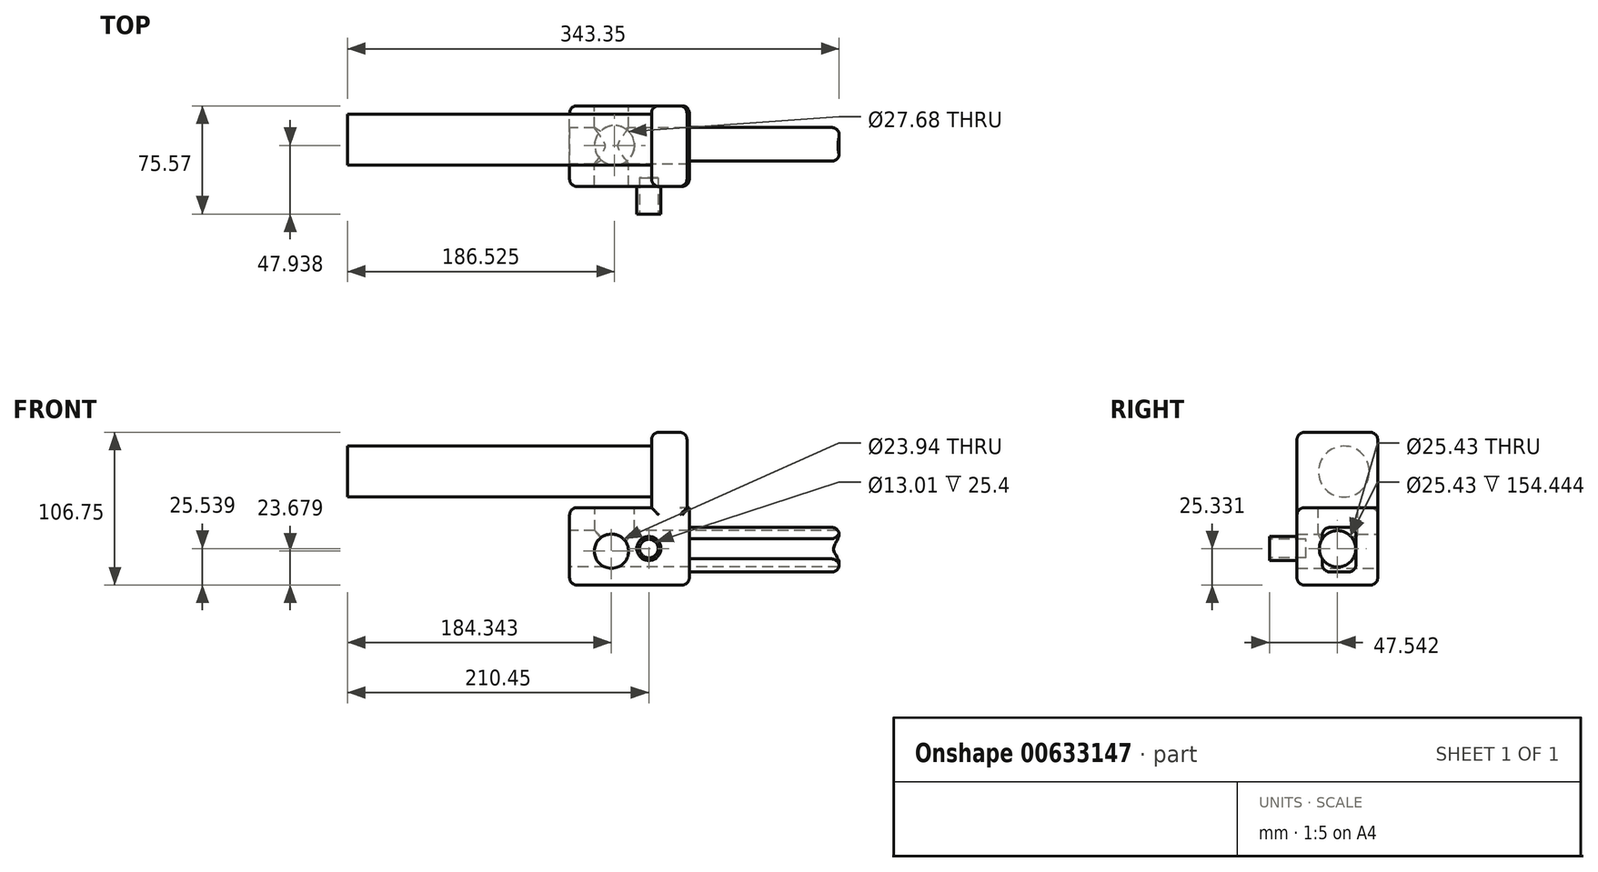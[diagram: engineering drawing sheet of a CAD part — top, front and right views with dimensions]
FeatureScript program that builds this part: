
annotation { "Feature Type Name" : "Feature", "Feature Type Description" : "" }
export const myFeature = defineFeature(function(context is Context, id is Id, definition is map)
    precondition{}
    {
        {
            var Q0;
            Q0=qCreatedBy(makeId("Front.planeOp"),FACE);
            var sketch = newSketch(context, id + "F0", { "sketchPlane" : qUnion([Q0])});
            skLineSegment(sketch, "E0.bottom", {"start": v(-35.66, -9.17) * mm, "end": v(47.91, -9.17) * mm});
            skLineSegment(sketch, "E0.top", {"start": v(-35.66, 44.89) * mm, "end": v(47.91, 44.89) * mm});
            skLineSegment(sketch, "E0.left", {"start": v(-35.66, -9.17) * mm, "end": v(-35.66, 44.89) * mm});
            skLineSegment(sketch, "E0.right", {"start": v(47.91, -9.17) * mm, "end": v(47.91, 44.89) * mm});
            skLineSegment(sketch, "E1.bottom", {"start": v(21.55, 44.89) * mm, "end": v(46.28, 44.89) * mm});
            skLineSegment(sketch, "E1.top", {"start": v(21.55, 97.58) * mm, "end": v(46.28, 97.58) * mm});
            skLineSegment(sketch, "E1.left", {"start": v(21.55, 44.89) * mm, "end": v(21.55, 97.58) * mm});
            skLineSegment(sketch, "E1.right", {"start": v(46.28, 44.89) * mm, "end": v(46.28, 97.58) * mm});
            skSolve(sketch);
        }
        {
            var Q0;
            Q0 = qSketchRegion(id + "F0", true);
            extrude(context, id + "F1", {"entities" : qUnion([Q0]), "depth" : 56.33 * mm, "offsetDistance" : 25.4 * mm});
        }
        {
            var Q0;
            Q0=makeQuery(id+"F1.opExtrude","CAP_EDGE",EDGE,{"disambiguationData":[OSD([sQuery(id+"F0.wireOp",EDGE,"E1.left")])],"isStart":false});
            var Q1;
            Q1=makeQuery(id+"F1.opExtrude","CAP_EDGE",EDGE,{"disambiguationData":[OSD([sQuery(id+"F0.wireOp",EDGE,"E1.right")])],"isStart":false});
            var Q2;
            Q2=makeQuery(id+"F1.opExtrude","CAP_EDGE",EDGE,{"disambiguationData":[OSD([sQuery(id+"F0.wireOp",EDGE,"E1.right")])],"isStart":true});
            var Q3;
            Q3=makeQuery(id+"F1.opExtrude","CAP_EDGE",EDGE,{"disambiguationData":[OSD([sQuery(id+"F0.wireOp",EDGE,"E1.left")])],"isStart":true});
            var Q4;
            Q4=makeQuery(id+"F1.opExtrude","CAP_EDGE",EDGE,{"disambiguationData":[OSD([sQuery(id+"F0.wireOp",EDGE,"E0.bottom")])],"isStart":false});
            var Q5;
            Q5=makeQuery(id+"F1.opExtrude","CAP_FACE",FACE,{"disambiguationData":[OSD([sQuery(id+"F0.wireOp",EDGE,"E0.bottom"),sQuery(id+"F0.wireOp",EDGE,"E0.top"),sQuery(id+"F0.wireOp",EDGE,"E0.left"),sQuery(id+"F0.wireOp",EDGE,"E0.right"),sQuery(id+"F0.wireOp",EDGE,"E1.top"),sQuery(id+"F0.wireOp",EDGE,"E1.left"),sQuery(id+"F0.wireOp",EDGE,"E1.right")])],"isStart":false});
            var Q6;
            Q6=makeQuery(id+"F1.opExtrude","CAP_EDGE",EDGE,{"disambiguationData":[OSD([sQuery(id+"F0.wireOp",EDGE,"E0.left")])],"isStart":true});
            var Q7;
            Q7=makeQuery(id+"F1.opExtrude","SWEPT_EDGE",EDGE,{"disambiguationData":[OSD([sQuery(id+"F0.wireOp",EDGE,"E1.top"),sQuery(id+"F0.wireOp",EDGE,"E1.left")])]});
            var Q8;
            Q8=makeQuery(id+"F1.opExtrude","SWEPT_EDGE",EDGE,{"disambiguationData":[OSD([sQuery(id+"F0.wireOp",EDGE,"E1.top"),sQuery(id+"F0.wireOp",EDGE,"E1.right")])]});
            fillet(context, id + "F2", {"entities" : qUnion([Q0, Q1, Q2, Q3, Q4, Q5, Q6, Q7, Q8]), "radius" : 5.08 * mm, "tangentPropagation" : true, "allowEdgeOverflow" : false});
        }
        {
            var Q0;
            Q0=makeQuery(id+"F1.opExtrude","CAP_EDGE",EDGE,{"disambiguationData":[OSD([sQuery(id+"F0.wireOp",EDGE,"E0.bottom")])],"isStart":true});
            var Q1;
            Q1=makeQuery(id+"F1.opExtrude","SWEPT_EDGE",EDGE,{"disambiguationData":[OSD([sQuery(id+"F0.wireOp",EDGE,"E0.bottom"),sQuery(id+"F0.wireOp",EDGE,"E0.right")])]});
            var Q2;
            Q2=makeQuery(id+"F1.opExtrude","SWEPT_EDGE",EDGE,{"disambiguationData":[OSD([sQuery(id+"F0.wireOp",EDGE,"E0.bottom"),sQuery(id+"F0.wireOp",EDGE,"E0.left")])]});
            fillet(context, id + "F3", {"entities" : qUnion([Q0, Q1, Q2]), "radius" : 5.08 * mm, "tangentPropagation" : true, "allowEdgeOverflow" : false});
        }
        {
            var Q0;
            Q0=makeQuery(id+"F1.opExtrude","CAP_FACE",FACE,{"disambiguationData":[OSD([sQuery(id+"F0.wireOp",EDGE,"E0.bottom"),sQuery(id+"F0.wireOp",EDGE,"E0.top"),sQuery(id+"F0.wireOp",EDGE,"E0.left"),sQuery(id+"F0.wireOp",EDGE,"E0.right"),sQuery(id+"F0.wireOp",EDGE,"E1.top"),sQuery(id+"F0.wireOp",EDGE,"E1.left"),sQuery(id+"F0.wireOp",EDGE,"E1.right")])],"isStart":true});
            var sketch = newSketch(context, id + "F4", { "sketchPlane" : qUnion([Q0])});
            skCircle(sketch, "E2", {"center": v(-20.36, 19.85) * mm, "radius": 0.17 * mm});
            skCircle(sketch, "E3", {"center": v(-19.66, 16.37) * mm, "radius": 8.38 * mm});
            skSolve(sketch);
        }
        {
            var Q0;
            Q0=makeQuery(id+"F4.imprint","IMPRINT",FACE,{"disambiguationData":[TD([[makeQuery(id+"F4.imprint","IMPRINT",EDGE,{"derivedFrom":sQuery(id+"F4.wireOp",EDGE,"E2")}),-1.0]])]});
            extrude(context, id + "F5", {"entities" : qUnion([Q0]), "operationType" : NewBodyOperationType.ADD, "oppositeDirection" : true, "depth" : 75.57 * mm, "offsetDistance" : 25.4 * mm});
        }
        {
            var Q0;
            Q0=makeQuery(id+"F5.opExtrude","CAP_FACE",FACE,{"disambiguationData":[OSD([sQuery(id+"F4.wireOp",EDGE,"E2"),sQuery(id+"F4.wireOp",EDGE,"E3")])],"isStart":false});
            var sketch = newSketch(context, id + "F6", { "sketchPlane" : qUnion([Q0])});
            skCircle(sketch, "E4", {"center": v(19.66, 16.37) * mm, "radius": 6.5 * mm});
            skSolve(sketch);
        }
        {
            var Q0;
            Q0 = qSketchRegion(id + "F6", true);
            extrude(context, id + "F7", {"entities" : qUnion([Q0]), "operationType" : NewBodyOperationType.REMOVE, "oppositeDirection" : true, "depth" : 25.4 * mm, "offsetDistance" : 25.4 * mm});
        }
        {
            var Q0;
            Q0=makeQuery(id+"F1.opExtrude","CAP_EDGE",EDGE,{"disambiguationData":[OSD([sQuery(id+"F0.wireOp",EDGE,"E1.top")])],"isStart":true});
            fillet(context, id + "F8", {"entities" : qUnion([Q0]), "radius" : 5.08 * mm, "tangentPropagation" : true, "allowEdgeOverflow" : false});
        }
        {
            var Q0;
            Q0=makeQuery(id+"F1.opExtrude","CAP_EDGE",EDGE,{"disambiguationData":[OSD([sQuery(id+"F0.wireOp",EDGE,"E0.right")])],"isStart":true});
            fillet(context, id + "F9", {"entities" : qUnion([Q0]), "radius" : 5.08 * mm, "tangentPropagation" : true, "allowEdgeOverflow" : false});
        }
        {
            var Q0;
            {var subQ0=sQuery(id+"F0.wireOp",EDGE,"E0.top");Q0=makeQuery(id+"F1.opExtrude","CAP_EDGE",EDGE,{"disambiguationData":[OSD([subQ0]),TDD([makeQuery(id+"F0.imprint","IMPRINT",EDGE,{"disambiguationData":[TD([[makeQuery(id+"F0.imprint","INTERSECT",VERTEX,{"derivedFrom":[subQ0,sQuery(id+"F0.wireOp",EDGE,"E0.left")]}),-1.0]])],"derivedFrom":subQ0})])],"isStart":true});}
            fillet(context, id + "F10", {"entities" : qUnion([Q0]), "radius" : 5.08 * mm, "tangentPropagation" : true, "allowEdgeOverflow" : false});
        }
        {
            var Q0;
            Q0=makeQuery(id+"F1.opExtrude","SWEPT_FACE",FACE,{"disambiguationData":[OSD([sQuery(id+"F0.wireOp",EDGE,"E0.right")])]});
            var sketch = newSketch(context, id + "F11", { "sketchPlane" : qUnion([Q0])});
            skSolve(sketch);
        }
        {
            var Q0;
            {var subQ0=sQuery(id+"F0.wireOp",EDGE,"E0.right");var subQ1=makeQuery(id+"F1.opExtrude","SWEPT_FACE",FACE,{"disambiguationData":[OSD([subQ0])]});Q0=makeQuery(id+"F11.imprint","IMPRINT",FACE,{"disambiguationData":[TD([[makeQuery(id+"F11.imprint","IMPRINT",EDGE,{"derivedFrom":makeQuery(id+"F2.opFillet","BLEND_EDGE",EDGE,{"blendedFrom":[makeQuery(id+"F1.opExtrude","CAP_EDGE",EDGE,{"disambiguationData":[OSD([subQ0])],"isStart":false}),subQ1],"blendedInto":[subQ1]})}),1.0]])]});}
            var sketch = newSketch(context, id + "F12", { "sketchPlane" : qUnion([Q0])});
            skLineSegment(sketch, "E5.bottom", {"start": v(-38.61, 31.08) * mm, "end": v(-15.2, 31.08) * mm});
            skLineSegment(sketch, "E5.top", {"start": v(-38.61, 0) * mm, "end": v(-15.2, 0) * mm});
            skLineSegment(sketch, "E5.left", {"start": v(-38.61, 31.08) * mm, "end": v(-38.61, 0) * mm});
            skLineSegment(sketch, "E5.right", {"start": v(-15.2, 31.08) * mm, "end": v(-15.2, 0) * mm});
            skSolve(sketch);
        }
        {
            var Q0;
            Q0 = qSketchRegion(id + "F12", true);
            extrude(context, id + "F13", {"entities" : qUnion([Q0]), "operationType" : NewBodyOperationType.ADD, "depth" : 104.65 * mm, "offsetDistance" : 25.4 * mm});
        }
        {
            var Q0;
            Q0=makeQuery(id+"F13.opExtrude","CAP_EDGE",EDGE,{"disambiguationData":[OSD([sQuery(id+"F12.wireOp",EDGE,"E5.left")])],"isStart":false});
            var Q1;
            Q1=makeQuery(id+"F13.opExtrude","CAP_EDGE",EDGE,{"disambiguationData":[OSD([sQuery(id+"F12.wireOp",EDGE,"E5.bottom")])],"isStart":false});
            var Q2;
            Q2=makeQuery(id+"F13.opExtrude","CAP_EDGE",EDGE,{"disambiguationData":[OSD([sQuery(id+"F12.wireOp",EDGE,"E5.right")])],"isStart":false});
            var Q3;
            Q3=makeQuery(id+"F13.opExtrude","CAP_EDGE",EDGE,{"disambiguationData":[OSD([sQuery(id+"F12.wireOp",EDGE,"E5.top")])],"isStart":false});
            var Q4;
            Q4=makeQuery(id+"F13.opExtrude","SWEPT_EDGE",EDGE,{"disambiguationData":[OSD([sQuery(id+"F12.wireOp",EDGE,"E5.bottom"),sQuery(id+"F12.wireOp",EDGE,"E5.left")])]});
            var Q5;
            Q5=makeQuery(id+"F13.opExtrude","SWEPT_EDGE",EDGE,{"disambiguationData":[OSD([sQuery(id+"F12.wireOp",EDGE,"E5.bottom"),sQuery(id+"F12.wireOp",EDGE,"E5.right")])]});
            var Q6;
            Q6=makeQuery(id+"F13.opExtrude","SWEPT_EDGE",EDGE,{"disambiguationData":[OSD([sQuery(id+"F12.wireOp",EDGE,"E5.top"),sQuery(id+"F12.wireOp",EDGE,"E5.left")])]});
            var Q7;
            Q7=makeQuery(id+"F13.opExtrude","SWEPT_EDGE",EDGE,{"disambiguationData":[OSD([sQuery(id+"F12.wireOp",EDGE,"E5.top"),sQuery(id+"F12.wireOp",EDGE,"E5.right")])]});
            fillet(context, id + "F14", {"entities" : qUnion([Q0, Q1, Q2, Q3, Q4, Q5, Q6, Q7]), "radius" : 5.08 * mm, "tangentPropagation" : true, "allowEdgeOverflow" : false});
        }
        {
            var Q0;
            Q0=makeQuery(id+"F1.opExtrude","CAP_FACE",FACE,{"disambiguationData":[OSD([sQuery(id+"F0.wireOp",EDGE,"E0.bottom"),sQuery(id+"F0.wireOp",EDGE,"E0.top"),sQuery(id+"F0.wireOp",EDGE,"E0.left"),sQuery(id+"F0.wireOp",EDGE,"E0.right"),sQuery(id+"F0.wireOp",EDGE,"E1.top"),sQuery(id+"F0.wireOp",EDGE,"E1.left"),sQuery(id+"F0.wireOp",EDGE,"E1.right")])],"isStart":true});
            var sketch = newSketch(context, id + "F15", { "sketchPlane" : qUnion([Q0])});
            skCircle(sketch, "E6", {"center": v(6.45, 14.5) * mm, "radius": 11.97 * mm});
            skSolve(sketch);
        }
        {
            var Q0;
            Q0 = qSketchRegion(id + "F15", true);
            extrude(context, id + "F16", {"entities" : qUnion([Q0]), "operationType" : NewBodyOperationType.REMOVE, "oppositeDirection" : true, "depth" : 79.25 * mm, "offsetDistance" : 25.4 * mm});
        }
        {
            var Q0;
            {var subQ0=sQuery(id+"F0.wireOp",EDGE,"E0.top");Q0=makeQuery(id+"F1.opExtrude","SWEPT_FACE",FACE,{"disambiguationData":[OSD([subQ0]),TDD([makeQuery(id+"F0.imprint","IMPRINT",EDGE,{"disambiguationData":[TD([[makeQuery(id+"F0.imprint","INTERSECT",VERTEX,{"derivedFrom":[subQ0,sQuery(id+"F0.wireOp",EDGE,"E0.left")]}),-1.0]])],"derivedFrom":subQ0})])]});}
            var sketch = newSketch(context, id + "F17", { "sketchPlane" : qUnion([Q0])});
            skCircle(sketch, "E7", {"center": v(-4.27, -27.63) * mm, "radius": 13.84 * mm});
            skSolve(sketch);
        }
        {
            var Q0;
            Q0 = qSketchRegion(id + "F17", true);
            extrude(context, id + "F18", {"entities" : qUnion([Q0]), "operationType" : NewBodyOperationType.REMOVE, "oppositeDirection" : true, "depth" : 25.4 * mm, "offsetDistance" : 25.4 * mm});
        }
        {
            var Q0;
            Q0=makeQuery(id+"F1.opExtrude","SWEPT_FACE",FACE,{"disambiguationData":[OSD([sQuery(id+"F0.wireOp",EDGE,"E0.left")])]});
            var sketch = newSketch(context, id + "F19", { "sketchPlane" : qUnion([Q0])});
            skCircle(sketch, "E8", {"center": v(28.03, 16.16) * mm, "radius": 12.72 * mm});
            skSolve(sketch);
        }
        {
            var Q0;
            Q0 = qSketchRegion(id + "F19", true);
            extrude(context, id + "F20", {"entities" : qUnion([Q0]), "operationType" : NewBodyOperationType.REMOVE, "oppositeDirection" : true, "depth" : 197.87 * mm, "offsetDistance" : 25.4 * mm});
        }
        {
            var Q0;
            Q0=makeQuery(id+"F1.opExtrude","SWEPT_FACE",FACE,{"disambiguationData":[OSD([sQuery(id+"F0.wireOp",EDGE,"E1.left")])]});
            var sketch = newSketch(context, id + "F21", { "sketchPlane" : qUnion([Q0])});
            skCircle(sketch, "E9", {"center": v(23.6, 70.12) * mm, "radius": 17.8 * mm});
            skSolve(sketch);
        }
        {
            var Q0;
            Q0 = qSketchRegion(id + "F21", true);
            extrude(context, id + "F22", {"entities" : qUnion([Q0]), "operationType" : NewBodyOperationType.ADD, "depth" : 212.34 * mm, "offsetDistance" : 25.4 * mm});
        }
    });
